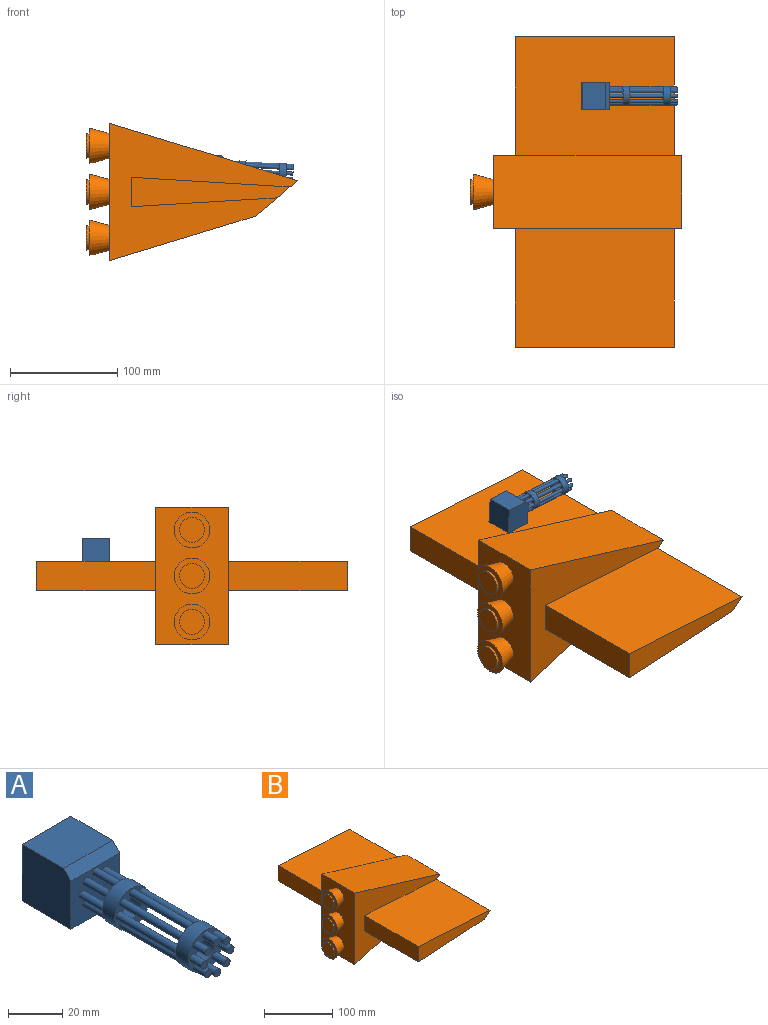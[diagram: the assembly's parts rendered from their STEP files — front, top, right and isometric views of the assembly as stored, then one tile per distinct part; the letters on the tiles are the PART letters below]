
ASSEMBLY  parts=2 mates=1
PART A: 47 faces, bbox 25.4x88.9x25.4 mm
  f0: cylinder r=1.59mm len=31.75mm, axis (0,1,0), area 316.7mm2, adj f10,f31
  f1: cylinder r=1.59mm len=31.75mm, axis (0,1,0), area 316.7mm2, adj f10,f31
  f2: cylinder r=1.59mm len=31.75mm, axis (0,1,0), area 316.7mm2, adj f10,f31
  f3: cylinder r=1.59mm len=31.75mm, axis (0,1,0), area 316.7mm2, adj f10,f31
  f4: cylinder r=1.59mm len=31.75mm, axis (0,1,0), area 316.7mm2, adj f10,f31
  f5: cylinder r=1.59mm len=31.75mm, axis (0,1,0), area 316.7mm2, adj f10,f31
  f6: cylinder r=1.59mm len=31.75mm, axis (0,1,0), area 316.7mm2, adj f10,f31
  f7: cylinder r=1.59mm len=31.75mm, axis (0,1,0), area 316.7mm2, adj f10,f31
  f8: cylinder r=4.8mm len=9.61mm, axis (0,-1,0), area 191.7mm2, adj f10,f11
  f9: cylinder r=9.02mm len=18.04mm, axis (0,-1,0), area 360mm2, adj f10,f11
  f10: plane 18.04x18.04mm, normal (0,1,0), area 119.9mm2, adj f0,f1,f2,f3,f4,f5,f6,f7
  f11: plane 18.04x18.04mm, normal (0,-1,0), area 119.9mm2, adj f8,f9,f13,f15,f17,f19,f21,f23
  f12: plane 3.18x3.18mm, normal (0,-1,0), area 7.9mm2, adj f13
  f13: cylinder r=1.59mm len=6.35mm, axis (0,1,0), area 63.3mm2, adj f11,f12
  f14: plane 3.18x3.18mm, normal (0,-1,0), area 7.9mm2, adj f15
  f15: cylinder r=1.59mm len=6.35mm, axis (0,1,0), area 63.3mm2, adj f11,f14
  f16: plane 3.18x3.18mm, normal (0,-1,0), area 7.9mm2, adj f17
  f17: cylinder r=1.59mm len=6.35mm, axis (0,1,0), area 63.3mm2, adj f11,f16
  f18: plane 3.18x3.18mm, normal (0,-1,0), area 7.9mm2, adj f19
  f19: cylinder r=1.59mm len=6.35mm, axis (0,1,0), area 63.3mm2, adj f11,f18
  f20: plane 3.18x3.18mm, normal (0,-1,0), area 7.9mm2, adj f21
  f21: cylinder r=1.59mm len=6.35mm, axis (0,1,0), area 63.3mm2, adj f11,f20
  f22: plane 3.18x3.18mm, normal (0,-1,0), area 7.9mm2, adj f23
  f23: cylinder r=1.59mm len=6.35mm, axis (0,1,0), area 63.3mm2, adj f11,f22
  f24: plane 3.18x3.18mm, normal (0,-1,0), area 7.9mm2, adj f25
  f25: cylinder r=1.59mm len=6.35mm, axis (0,1,0), area 63.3mm2, adj f11,f24
  f26: plane 3.18x3.18mm, normal (0,-1,0), area 7.9mm2, adj f27
  f27: cylinder r=1.59mm len=6.35mm, axis (0,1,0), area 63.3mm2, adj f11,f26
  f28: cylinder r=4.8mm len=9.61mm, axis (0,-1,0), area 191.7mm2, adj f30,f31
  f29: cylinder r=9.02mm len=18.04mm, axis (0,-1,0), area 360mm2, adj f30,f31
  f30: plane 18.04x18.04mm, normal (0,1,0), area 119.9mm2, adj f28,f29,f37,f38,f39,f40,f41,f42
  f31: plane 18.04x18.04mm, normal (0,-1,0), area 119.9mm2, adj f0,f1,f2,f3,f4,f5,f6,f7
  f32: plane 25.4x25.4mm, normal (0,1,0), area 645.2mm2, adj f33,f34,f35,f36
  f33: plane 25.4x25.4mm, normal (-1,0,0), area 637.9mm2, adj f32,f34,f36,f44,f46
  f34: plane 25.4x21.59mm, normal (0,0,1), area 548.4mm2, adj f32,f33,f35,f46
  f35: plane 25.4x25.4mm, normal (1,0,0), area 637.9mm2, adj f32,f34,f36,f44,f46
  f36: plane 25.4x25.4mm, normal (0,0,-1), area 645.2mm2, adj f32,f33,f35,f44
  f37: cylinder r=1.59mm len=12.7mm, axis (0,1,0), area 126.7mm2, adj f30,f44
  f38: cylinder r=1.59mm len=12.7mm, axis (0,1,0), area 126.7mm2, adj f30,f44
  f39: cylinder r=1.59mm len=12.7mm, axis (0,1,0), area 126.7mm2, adj f30,f44
  f40: cylinder r=1.59mm len=12.7mm, axis (0,1,0), area 126.7mm2, adj f30,f44
  f41: cylinder r=1.59mm len=12.7mm, axis (0,1,0), area 126.7mm2, adj f30,f44
  f42: cylinder r=1.59mm len=12.7mm, axis (0,1,0), area 126.7mm2, adj f30,f44
  f43: cylinder r=1.59mm len=12.7mm, axis (0,1,0), area 126.7mm2, adj f30,f44
  f44: plane 25.4x21.59mm, normal (0,-1,0), area 485mm2, adj f33,f35,f36,f37,f38,f39,f40,f41
  f45: cylinder r=1.59mm len=12.7mm, axis (0,1,0), area 126.7mm2, adj f30,f44
  f46: plane 25.4x3.81mm, normal (0,-0.71,0.71), area 136.9mm2, adj f33,f34,f35,f44
PART B: 26 faces, bbox 197.1x290.1x128.2 mm
  f0: plane 175.48x128.15mm, normal (0,-1,0), area 10006.7mm2, adj f2,f3,f4,f5,f10,f11,f12
  f1: plane 175.48x128.15mm, normal (0,1,0), area 10006.7mm2, adj f2,f3,f4,f5,f7,f8,f9
  f2: plane 135.79x68.07mm, normal (0.29,0,-0.96), area 9663.5mm2, adj f0,f1,f3,f5
  f3: plane 290.07x39.68mm, normal (0.64,0,-0.77), area 7039mm2, adj f0,f1,f2,f4,f6,f7,f9,f10
  f4: plane 175.48x68.07mm, normal (0.29,0,0.96), area 12487.5mm2, adj f0,f1,f3,f5
  f5: plane 128.15x68.07mm, normal (-1,0,0), area 7471.5mm2, adj f0,f1,f2,f4,f14,f16,f18
  f6: plane 148.23x27.46mm, normal (0,1,0), area 2677.3mm2, adj f3,f7,f8,f9
  f7: plane 136.11x111mm, normal (0.06,0,-1), area 15135.6mm2, adj f1,f3,f6,f8
  f8: plane 111x27.46mm, normal (-1,0,0), area 3048.2mm2, adj f1,f6,f7,f9
  f9: plane 148.23x111mm, normal (0.06,0,1), area 16483.5mm2, adj f1,f3,f6,f8
  f10: plane 148.23x111mm, normal (0.06,0,1), area 16483.5mm2, adj f0,f3,f11,f13
  f11: plane 111x27.46mm, normal (-1,0,0), area 3048.2mm2, adj f0,f10,f12,f13
  f12: plane 136.11x111mm, normal (0.06,0,-1), area 15135.6mm2, adj f0,f3,f11,f13
  f13: plane 148.23x27.46mm, normal (0,-1,0), area 2677.3mm2, adj f3,f10,f11,f12
  f14: cone r=11.53mm half-angle=15deg, axis (-1,0,0), area 1744.6mm2, adj f5,f15
  f15: plane 33.26x33.26mm, normal (-1,0,0), area 451.5mm2, adj f14,f20
  f16: cone r=11.53mm half-angle=15deg, axis (-1,0,0), area 1744.6mm2, adj f5,f17
  f17: plane 33.26x33.26mm, normal (-1,0,0), area 451.5mm2, adj f16,f22
  f18: cone r=11.53mm half-angle=15deg, axis (-1,0,0), area 1744.6mm2, adj f5,f19
  f19: plane 33.26x33.26mm, normal (-1,0,0), area 451.5mm2, adj f18,f24
  f20: cylinder r=11.53mm len=23.05mm, axis (1,0,0), area 184mm2, adj f15,f21
  f21: plane 23.05x23.05mm, normal (-1,0,0), area 417.4mm2, adj f20
  f22: cylinder r=11.53mm len=23.05mm, axis (1,0,0), area 184mm2, adj f17,f23
  f23: plane 23.05x23.05mm, normal (-1,0,0), area 417.4mm2, adj f22
  f24: cylinder r=11.53mm len=23.05mm, axis (1,0,0), area 184mm2, adj f19,f25
  f25: plane 23.05x23.05mm, normal (-1,0,0), area 417.4mm2, adj f24
PLACE A rot(axis=(0.03,0.03,1),90.1deg) t=(7.99,89.53,9.22)mm
PLACE B at identity fixed
MATE fastened A.f36 <-> B.f9  axis (-0.06,0,-1) through (7.99,89.53,9.22)mm
